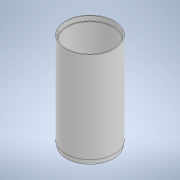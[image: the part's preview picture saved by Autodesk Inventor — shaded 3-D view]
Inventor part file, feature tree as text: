
AUTODESK INVENTOR PART (.ipt)
format: ipt  version: 2020.3 (Build 243373000, 373)  size: 271,360 bytes
history: native  units: mm
features: extrude x6, sketch x5, plane x2, chamfer x2, projected_geometry x2, pattern_circular x1, split x1
ambient origin geometry x8: Origin, YZ Plane, XZ Plane, XY Plane, X Axis, Y Axis, Z Axis, Center Point
bodies: Solid1 (feature_tree), Solid2 (feature_tree), Solid3 (feature_tree)
feature tree (19):
  sketch  "Sketch1"  dims[d0=50.0mm d1=51.8mm]
  extrude  "Extrusion1"  Depth=50.0mm
  extrude  "Extrusion2"  Depth=75.0mm TaperAngle=0.0deg
  extrude  "Extrusion4"  Depth=75.0mm
  plane  "Work Plane1"
  extrude  "Extrusion5"  Depth=50.0mm
  chamfer  "Chamfer1"  Distance=3.6mm
  chamfer  "Chamfer2"  Distance=175.0mm
  pattern_circular  "Circular Pattern3"  [2 undecoded]
  plane  "Work Plane2"
  split  "Split1"
  extrude  "Extrusion6"  [1 undecoded]
  extrude  "Extrusion7"  Depth=5.0mm TaperAngle=45.0deg
  sketch  "Sketch4"  dims[d2=53.6mm d3=75.0mm d4=180.0mm d5=0.0mm d6=0.0mm]
  projected_geometry  "Projected Loop1"
  sketch  "Sketch7"  dims[d21=9.930923mm d24=50.0mm]
  sketch  "Sketch8"  dims[d25=55.0mm d26=3.6mm d27=0.0mm d31=175.0mm d32=0.0mm d33=5.0mm d34=-125.0mm d35=50.0mm d36=51.8mm d37=53.6mm d38=5.0mm d39=5.0mm d40=0.0mm d41=1.8mm d42=2.0mm d43=45.0deg d44=1.8mm d45=2.0mm d46=45.0deg d47=30.0mm d48=360.0deg d50=-75.0mm d51=50.0mm d52=51.8mm d53=5.0mm d54=0.0mm d55=50.0mm d56=51.8mm d57=5.0mm d58=0.0mm d11=0.5mm d12=0.872665mm d13=0.5mm d14=0.872665mm]
  projected_geometry  "Project Cut Edges1"
  sketch  "Sketch5"  dims[d7=75.0mm d8=0.0mm d18=70.0mm]
note: 3 required parameter values undecoded (feature->parameter linkage not recoverable at this tier; creation-order binding heuristic only, values carry confidence <= 0.55)
